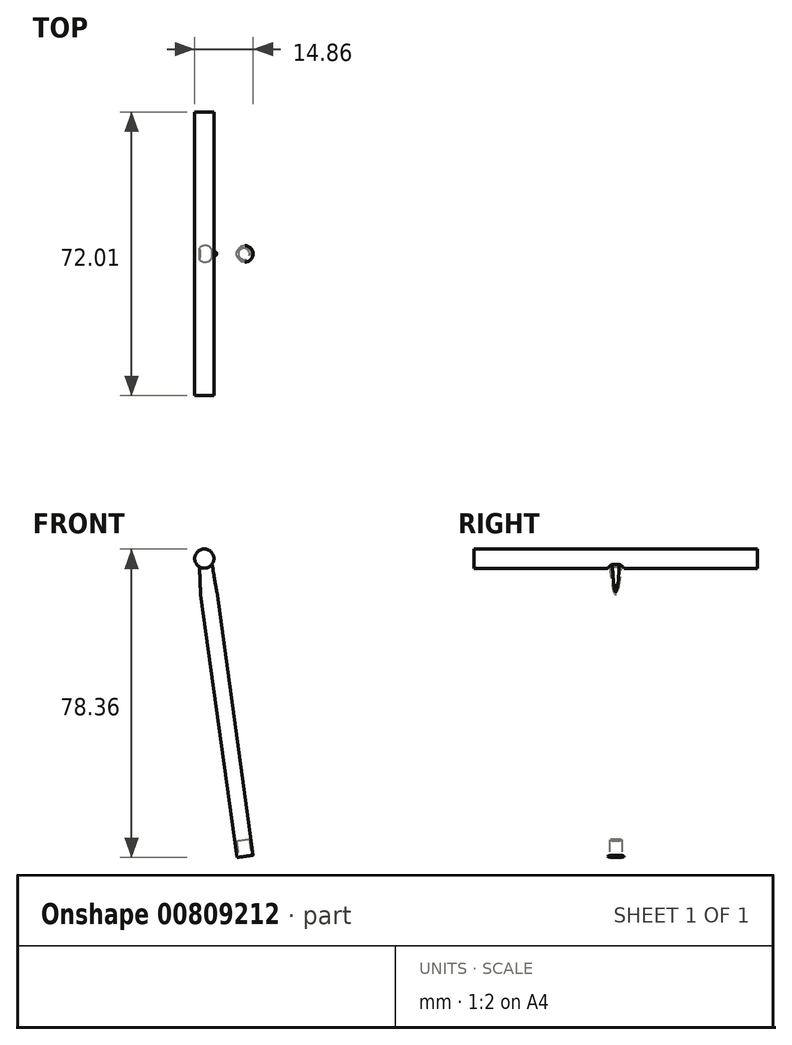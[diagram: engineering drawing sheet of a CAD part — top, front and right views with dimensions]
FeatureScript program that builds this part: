
annotation { "Feature Type Name" : "Feature", "Feature Type Description" : "" }
export const myFeature = defineFeature(function(context is Context, id is Id, definition is map)
    precondition{}
    {
        {
            var Q0;
            Q0=qCreatedBy(makeId("Front.planeOp"),FACE);
            var sketch = newSketch(context, id + "F0", { "sketchPlane" : qUnion([Q0])});
            skCircle(sketch, "E0", {"center": v(21.95, 57.9) * mm, "radius": 2.44 * mm});
            skLineSegment(sketch, "E1", {"start": v(21, 48.7) * mm, "end": v(30.22, -18.02) * mm});
            skLineSegment(sketch, "E2", {"start": v(30.22, -18.02) * mm, "end": v(34.37, -17.45) * mm});
            skLineSegment(sketch, "E3", {"start": v(34.37, -17.45) * mm, "end": v(25.12, 49.42) * mm});
            skLineSegment(sketch, "E4", {"start": v(21, 48.7) * mm, "end": v(25.12, 49.42) * mm});
            skLineSegment(sketch, "E5", {"start": v(23.93, 56.47) * mm, "end": v(25.12, 49.42) * mm});
            skLineSegment(sketch, "E6", {"start": v(20.74, 55.79) * mm, "end": v(21, 48.7) * mm});
            skSolve(sketch);
        }
        {
            var Q0;
            Q0=makeQuery(id+"F0.imprint","IMPRINT",FACE,{"disambiguationData":[TD([[makeQuery(id+"F0.imprint","IMPRINT",EDGE,{"derivedFrom":sQuery(id+"F0.wireOp",EDGE,"E1")}),1.0]])]});
            var Q1;
            {var subQ1=sQuery(id+"F0.wireOp",EDGE,"1oIaWiPY-Bf0m-q6P9-hbuv-pavkih47shiB");Q1=makeQuery(id+"F0.imprint","IMPRINT",FACE,{"disambiguationData":[TD([[makeQuery(id+"F0.imprint","IMPRINT",EDGE,{"derivedFrom":subQ1}),1.0]])]});}
            var Q2;
            Q2=makeQuery(id+"F0.imprint","IMPRINT",FACE,{"disambiguationData":[TD([[makeQuery(id+"F0.imprint","IMPRINT",EDGE,{"derivedFrom":sQuery(id+"F0.wireOp",EDGE,"E4")}),1.0]])]});
            extrude(context, id + "F1", {"entities" : qUnion([Q0, Q1, Q2]), "depth" : 4.2 * mm, "offsetDistance" : 25.4 * mm});
        }
        {
            var Q0;
            Q0=makeQuery(id+"F1.opExtrude","CAP_EDGE",EDGE,{"disambiguationData":[OSD([sQuery(id+"F0.wireOp",EDGE,"E3")])],"isStart":true});
            var Q1;
            Q1=makeQuery(id+"F1.opExtrude","CAP_EDGE",EDGE,{"disambiguationData":[OSD([sQuery(id+"F0.wireOp",EDGE,"E3")])],"isStart":false});
            var Q2;
            Q2=makeQuery(id+"F1.opExtrude","CAP_EDGE",EDGE,{"disambiguationData":[OSD([sQuery(id+"F0.wireOp",EDGE,"E1")])],"isStart":false});
            var Q3;
            Q3=makeQuery(id+"F1.opExtrude","CAP_EDGE",EDGE,{"disambiguationData":[OSD([sQuery(id+"F0.wireOp",EDGE,"E1")])],"isStart":true});
            fillet(context, id + "F2", {"entities" : qUnion([Q0, Q1, Q2, Q3]), "radius" : 2.1 * mm, "tangentPropagation" : true, "allowEdgeOverflow" : false});
        }
        {
            var Q0;
            {var subQ0=sQuery(id+"F0.wireOp",EDGE,"E0");var subQ1=makeQuery(id+"F0.imprint","INTERSECT",VERTEX,{"derivedFrom":[subQ0,sQuery(id+"F0.wireOp",EDGE,"E5")]});Q0=makeQuery(id+"F0.imprint","IMPRINT",FACE,{"disambiguationData":[TD([[makeQuery(id+"F0.imprint","IMPRINT",EDGE,{"disambiguationData":[TD([[subQ1,1.0]])],"derivedFrom":subQ0}),1.0]])]});}
            extrude(context, id + "F3", {"entities" : qUnion([Q0]), "operationType" : NewBodyOperationType.ADD, "depth" : 38.1 * mm, "offsetDistance" : 25.4 * mm});
        }
        {
            var Q0;
            {var subQ0=sQuery(id+"F0.wireOp",EDGE,"E0");var subQ1=makeQuery(id+"F0.imprint","INTERSECT",VERTEX,{"derivedFrom":[subQ0,sQuery(id+"F0.wireOp",EDGE,"E5")]});Q0=makeQuery(id+"F0.imprint","IMPRINT",FACE,{"disambiguationData":[TD([[makeQuery(id+"F0.imprint","IMPRINT",EDGE,{"disambiguationData":[TD([[subQ1,1.0]])],"derivedFrom":subQ0}),1.0]])]});}
            extrude(context, id + "F4", {"entities" : qUnion([Q0]), "operationType" : NewBodyOperationType.ADD, "oppositeDirection" : true, "depth" : 33.9 * mm, "offsetDistance" : 25.4 * mm});
        }
        {
            var Q0;
            Q0=makeQuery(id+"F1.opExtrude","SWEPT_FACE",FACE,{"disambiguationData":[OSD([sQuery(id+"F0.wireOp",EDGE,"E2")])]});
            var sketch = newSketch(context, id + "F5", { "sketchPlane" : qUnion([Q0])});
            skCircle(sketch, "E7", {"center": v(29.56, 2.1) * mm, "radius": 1.59 * mm});
            skSolve(sketch);
        }
        {
            var Q0;
            Q0=makeQuery(id+"F5.imprint","IMPRINT",FACE,{"disambiguationData":[TD([[makeQuery(id+"F5.imprint","IMPRINT",EDGE,{"derivedFrom":sQuery(id+"F5.wireOp",EDGE,"E7")}),1.0]])]});
            extrude(context, id + "F6", {"entities" : qUnion([Q0]), "operationType" : NewBodyOperationType.REMOVE, "oppositeDirection" : true, "depth" : 4.2 * mm, "offsetDistance" : 25.4 * mm});
        }
    });
